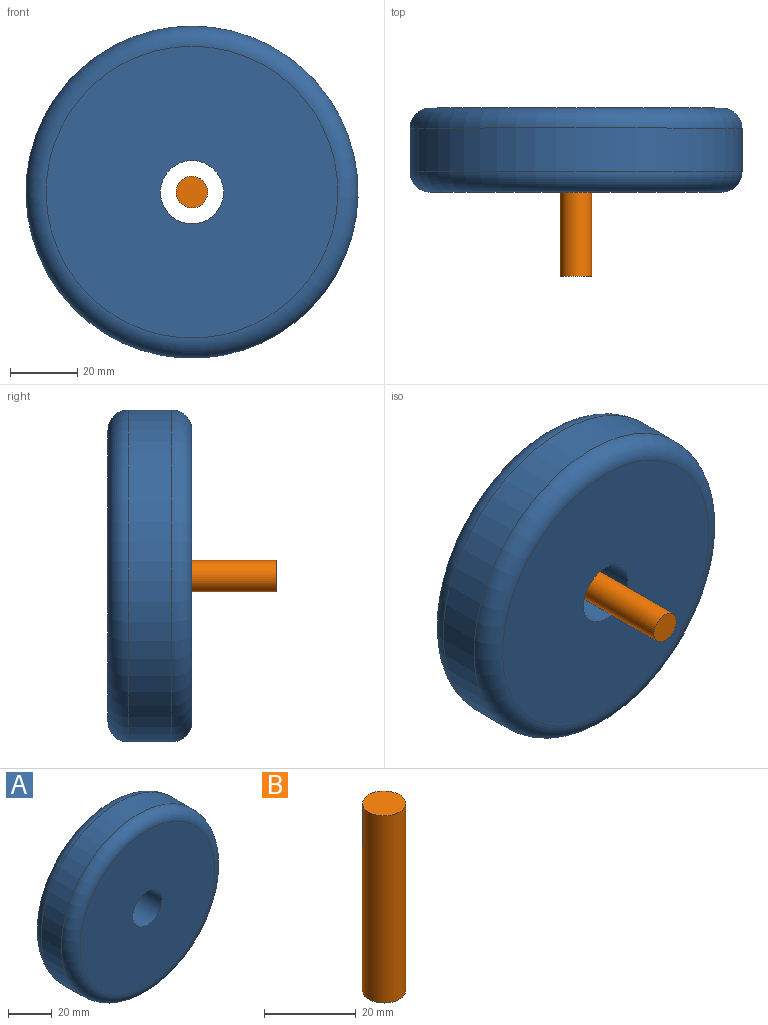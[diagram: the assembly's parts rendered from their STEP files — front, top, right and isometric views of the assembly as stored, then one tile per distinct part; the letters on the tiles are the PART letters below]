
ASSEMBLY  parts=2 mates=2
PART A: 12 faces, bbox 106.9x25x106.9 mm
  f0: plane 23.81x23.81mm, normal (0,1,0), area 167.3mm2, adj f3,f9
  f1: cylinder r=49.4mm len=98.81mm, axis (0,-1,0), area 4035.3mm2, adj f4,f5
  f2: plane 86.81x86.81mm, normal (0,-1,0), area 5640.5mm2, adj f3,f5
  f3: cylinder r=9.4mm len=25mm, axis (0,-1,0), area 1477.1mm2, adj f0,f2
  f4: torus R=43.4mm, axis (0,1,0), area 2796.4mm2, adj f1,f6
  f5: torus R=43.4mm, axis (0,1,0), area 2796.4mm2, adj f1,f2
  f6: cylinder r=43.4mm len=86.81mm, axis (0,1,0), area 681.8mm2, adj f4,f10
  f7: cylinder r=46.9mm len=93.81mm, axis (0,-1,0), area 3831.1mm2, adj f10,f11
  f8: plane 86.81x86.81mm, normal (0,1,0), area 5473.2mm2, adj f9,f11
  f9: cylinder r=11.9mm len=23.81mm, axis (0,-1,0), area 1682.8mm2, adj f0,f8
  f10: torus R=43.4mm, axis (0,1,0), area 1576.3mm2, adj f6,f7
  f11: torus R=43.4mm, axis (0,1,0), area 1576.3mm2, adj f7,f8
PART B: 3 faces, bbox 9.4x9.4x50 mm
  f0: cylinder r=4.7mm len=50mm, axis (0,0,-1), area 1476.5mm2, adj f1,f2
  f1: plane 9.4x9.4mm, normal (0,0,1), area 69.4mm2, adj f0
  f2: plane 9.4x9.4mm, normal (0,0,-1), area 69.4mm2, adj f0
PLACE A rot(axis=(0,0,1),0deg) t=(-26.83,-60.42,-29.15)mm
PLACE B rot(axis=(1,0,0),90deg) t=(-26.83,-27.84,-29.15)mm
MATE slider B.f0 <-> A.f1  axis (0,1,0) through (-26.83,-27.84,-29.15)mm
MATE planar B.f0 <-> A.f1  axis (0,1,0) through (-26.83,-27.84,-29.15)mm
